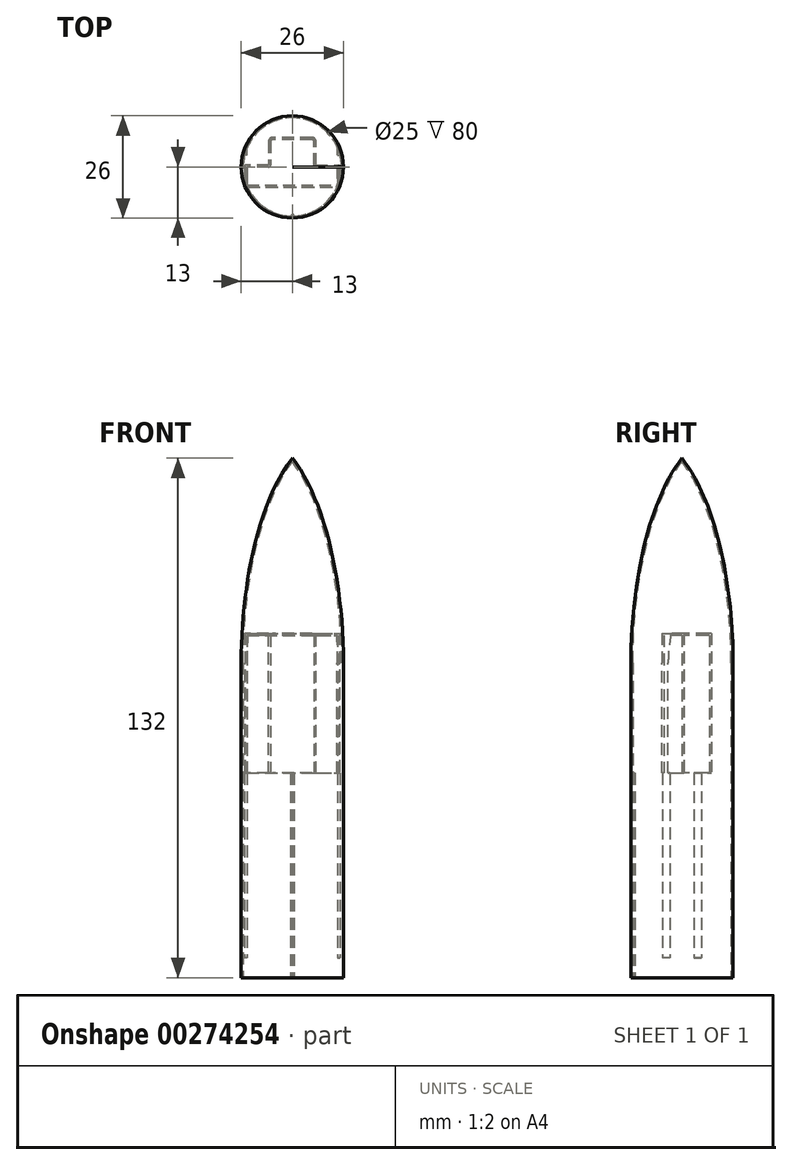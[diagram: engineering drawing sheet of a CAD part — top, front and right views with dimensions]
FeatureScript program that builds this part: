
annotation { "Feature Type Name" : "Feature", "Feature Type Description" : "" }
export const myFeature = defineFeature(function(context is Context, id is Id, definition is map)
    precondition{}
    {
        {
            var Q0;
            Q0=qCreatedBy(makeId("Top.planeOp"),FACE);
            var sketch = newSketch(context, id + "F0", { "sketchPlane" : qUnion([Q0])});
            skCircle(sketch, "E0", {"center": v(0, 0) * mm, "radius": 13 * mm});
            skSolve(sketch);
        }
        {
            var Q0;
            Q0=qCreatedBy(makeId("Front.planeOp"),FACE);
            var sketch = newSketch(context, id + "F1", { "sketchPlane" : qUnion([Q0])});
            skLineSegment(sketch, "E1", {"start": v(13, -80) * mm, "end": v(13, 0) * mm});
            skFitSpline(sketch, "E2", {"points": [v(13, 0) * mm, v(0, 52) * mm], "startDerivative": vector(0, 61.89) * mm, "endDerivative": vector(-24.62, 30.86) * mm});
            skLineSegment(sketch, "E3", {"start": v(0, 52) * mm, "end": v(0, 0) * mm});
            skLineSegment(sketch, "E4", {"start": v(13, -80) * mm, "end": v(0, -80) * mm});
            skLineSegment(sketch, "E5", {"start": v(0, 0) * mm, "end": v(0, -80) * mm});
            skSolve(sketch);
        }
        {
            var Q0;
            Q0 = qSketchRegion(id + "F1", true);
            var Q1;
            Q1=sQuery(id+"F1.wireOp",EDGE,"E3");
            revolve(context, id + "F2", {"entities" : qUnion([Q0]), "axis" : qUnion([Q1]), "revolveType" : RevolveType.FULL});
        }
        {
            var Q0;
            Q0=makeQuery(id+"F2.opRevolve","SWEPT_FACE",FACE,{"disambiguationData":[OSD([sQuery(id+"F1.wireOp",EDGE,"E4")])]});
            var sketch = newSketch(context, id + "F3", { "sketchPlane" : qUnion([Q0])});
            skCircle(sketch, "E6", {"center": v(0, 0) * mm, "radius": 4.6 * mm, "construction": true});
            skLineSegment(sketch, "E7", {"start": v(11.62, -4.6) * mm, "end": v(11.5, -4.6) * mm});
            skLineSegment(sketch, "E8", {"start": v(-11.62, 4.6) * mm, "end": v(-11.5, 4.6) * mm});
            skCircle(sketch, "E9", {"center": v(0, 0) * mm, "radius": 12.5 * mm});
            skLineSegment(sketch, "E10", {"start": v(0, 0) * mm, "end": v(11.5, 0) * mm});
            skLineSegment(sketch, "E11", {"start": v(0, 0) * mm, "end": v(-11.5, 0) * mm});
            skLineSegment(sketch, "E12", {"start": v(11.5, 3) * mm, "end": v(5.5, 3) * mm});
            skLineSegment(sketch, "E13", {"start": v(-11.5, 3) * mm, "end": v(-11.5, 0) * mm});
            skLineSegment(sketch, "E14", {"start": v(-11.5, 3) * mm, "end": v(-11.5, 4.6) * mm});
            skLineSegment(sketch, "E15", {"start": v(11.5, 3) * mm, "end": v(11.5, 0) * mm});
            skLineSegment(sketch, "E16", {"start": v(11.5, 3) * mm, "end": v(11.5, 4.6) * mm});
            skLineSegment(sketch, "E17", {"start": v(11.5, 0) * mm, "end": v(11.5, -3) * mm});
            skLineSegment(sketch, "E18", {"start": v(11.5, -3) * mm, "end": v(11.5, -4.6) * mm});
            skLineSegment(sketch, "E19", {"start": v(11.5, -3) * mm, "end": v(-11.5, -3) * mm, "construction": true});
            skLineSegment(sketch, "E20", {"start": v(-11.5, -3) * mm, "end": v(-11.5, 0) * mm});
            skLineSegment(sketch, "E21", {"start": v(-11.5, -3) * mm, "end": v(-11.5, -4.6) * mm});
            skCircle(sketch, "E22", {"center": v(0, 0) * mm, "radius": 13 * mm});
            skLineSegment(sketch, "E23", {"start": v(5.5, 3) * mm, "end": v(5.5, -7) * mm});
            skLineSegment(sketch, "E24", {"start": v(5.5, -7) * mm, "end": v(-5.5, -7) * mm});
            skLineSegment(sketch, "E25", {"start": v(-5.5, -7) * mm, "end": v(-5.5, 3) * mm});
            skLineSegment(sketch, "E26", {"start": v(0, 3) * mm, "end": v(-5.5, 3) * mm});
            skLineSegment(sketch, "E27", {"start": v(5.5, 3) * mm, "end": v(0, 3) * mm});
            skLineSegment(sketch, "E28", {"start": v(-5.5, 3) * mm, "end": v(-11.5, 3) * mm});
            skLineSegment(sketch, "E29", {"start": v(-11.5, 4.6) * mm, "end": v(-8.96, 4.6) * mm});
            skLineSegment(sketch, "E30", {"start": v(-11.5, -4.6) * mm, "end": v(-11.62, -4.6) * mm});
            skLineSegment(sketch, "E31", {"start": v(11.5, 4.6) * mm, "end": v(11.62, 4.6) * mm});
            skLineSegment(sketch, "E32", {"start": v(11.5, -4.6) * mm, "end": v(-11.5, -4.6) * mm});
            skLineSegment(sketch, "E33", {"start": v(8.96, 4.6) * mm, "end": v(11.5, 4.6) * mm});
            skLineSegment(sketch, "E34", {"start": v(-8.96, 4.6) * mm, "end": v(8.96, 4.6) * mm});
            skLineSegment(sketch, "E35", {"start": v(11.5, 0) * mm, "end": v(12.5, 0) * mm});
            skLineSegment(sketch, "E36", {"start": v(-11.5, 0) * mm, "end": v(-12.5, 0) * mm});
            skLineSegment(sketch, "E37", {"start": v(8.96, 4.6) * mm, "end": v(8.96, 5.6) * mm});
            skLineSegment(sketch, "E38", {"start": v(8.96, 5.6) * mm, "end": v(11.18, 5.6) * mm});
            skLineSegment(sketch, "E39", {"start": v(-8.96, 4.6) * mm, "end": v(-8.96, 5.6) * mm});
            skLineSegment(sketch, "E40", {"start": v(-8.96, 5.6) * mm, "end": v(-11.18, 5.6) * mm});
            skLineSegment(sketch, "E41", {"start": v(-11.5, -4.6) * mm, "end": v(-11.5, -4.9) * mm});
            skLineSegment(sketch, "E42", {"start": v(11.5, -4.6) * mm, "end": v(11.5, -4.9) * mm});
            skLineSegment(sketch, "E43", {"start": v(0, 12) * mm, "end": v(0.5, 12.5) * mm});
            skLineSegment(sketch, "E44", {"start": v(0.5, 12.5) * mm, "end": v(-0.5, 12.5) * mm});
            skLineSegment(sketch, "E45", {"start": v(-0.5, 12.5) * mm, "end": v(0, 12) * mm});
            skLineSegment(sketch, "E46", {"start": v(0, 0) * mm, "end": v(0, 12.5) * mm, "construction": true});
            skLineSegment(sketch, "E47", {"start": v(-11.5, 4.6) * mm, "end": v(-11.5, 4.9) * mm});
            skLineSegment(sketch, "E48", {"start": v(11.5, 4.6) * mm, "end": v(11.5, 4.9) * mm});
            skLineSegment(sketch, "E49", {"start": v(11.5, -3) * mm, "end": v(12.13, -3) * mm});
            skLineSegment(sketch, "E50", {"start": v(11.5, 3) * mm, "end": v(12.13, 3) * mm});
            skLineSegment(sketch, "E51", {"start": v(-11.5, -3) * mm, "end": v(-12.13, -3) * mm});
            skLineSegment(sketch, "E52", {"start": v(-11.5, 3) * mm, "end": v(-12.13, 3) * mm});
            skSolve(sketch);
        }
        {
            var Q0;
            Q0=makeQuery(id+"F3.imprint","IMPRINT",FACE,{"disambiguationData":[TD([[makeQuery(id+"F3.imprint","IMPRINT",EDGE,{"derivedFrom":sQuery(id+"F3.wireOp",EDGE,"E12")}),-1.0]])]});
            var Q1;
            {var subQ0=sQuery(id+"F3.wireOp",EDGE,"E13");Q1=makeQuery(id+"F3.imprint","IMPRINT",FACE,{"disambiguationData":[TD([[makeQuery(id+"F3.imprint","IMPRINT",EDGE,{"derivedFrom":subQ0}),1.0]])]});}
            var Q2;
            {var subQ4=sQuery(id+"F3.wireOp",EDGE,"E12");Q2=makeQuery(id+"F3.imprint","IMPRINT",FACE,{"disambiguationData":[TD([[makeQuery(id+"F3.imprint","IMPRINT",EDGE,{"derivedFrom":subQ4}),1.0]])]});}
            var Q3;
            {var subQ0=sQuery(id+"F3.wireOp",EDGE,"E26");Q3=makeQuery(id+"F3.imprint","IMPRINT",FACE,{"disambiguationData":[TD([[makeQuery(id+"F3.imprint","IMPRINT",EDGE,{"derivedFrom":subQ0}),1.0]])]});}
            var Q4;
            {var subQ1=sQuery(id+"F3.wireOp",EDGE,"E10");var subQ7=sQuery(id+"F3.wireOp",EDGE,"E11");var subQ8=makeQuery(id+"F3.imprint","INTERSECT",VERTEX,{"derivedFrom":[subQ1,subQ7]});Q4=makeQuery(id+"F3.imprint","IMPRINT",FACE,{"disambiguationData":[TD([[makeQuery(id+"F3.imprint","IMPRINT",EDGE,{"disambiguationData":[TD([[subQ8,-1.0]])],"derivedFrom":subQ1}),-1.0]])]});}
            var Q5;
            {var subQ0=sQuery(id+"F3.wireOp",EDGE,"E23");var subQ1=sQuery(id+"F3.wireOp",EDGE,"E19");var subQ2=makeQuery(id+"F3.imprint","INTERSECT",VERTEX,{"derivedFrom":[subQ1,subQ0]});Q5=makeQuery(id+"F3.imprint","IMPRINT",FACE,{"disambiguationData":[TD([[makeQuery(id+"F3.imprint","IMPRINT",EDGE,{"disambiguationData":[TD([[subQ2,-1.0]])],"derivedFrom":subQ1}),1.0]])]});}
            var Q6;
            {var subQ0=sQuery(id+"F3.wireOp",EDGE,"E24");Q6=makeQuery(id+"F3.imprint","IMPRINT",FACE,{"disambiguationData":[TD([[makeQuery(id+"F3.imprint","IMPRINT",EDGE,{"derivedFrom":subQ0}),-1.0]])]});}
            var Q7;
            {var subQ0=sQuery(id+"F3.wireOp",EDGE,"qLuiB2uP-4wZ7-qQD2-egaY-P2IEysGGcevB");Q7=makeQuery(id+"F3.imprint","IMPRINT",FACE,{"disambiguationData":[TD([[makeQuery(id+"F3.imprint","IMPRINT",EDGE,{"derivedFrom":subQ0}),-1.0]])]});}
            extrude(context, id + "F4", {"entities" : qUnion([Q0, Q1, Q2, Q3, Q4, Q5, Q6, Q7]), "operationType" : NewBodyOperationType.REMOVE, "oppositeDirection" : true, "depth" : 87 * mm});
        }
        {
            var Q0;
            {var subQ0=sQuery(id+"F3.wireOp",EDGE,"E17");Q0=makeQuery(id+"F3.imprint","IMPRINT",FACE,{"disambiguationData":[TD([[makeQuery(id+"F3.imprint","IMPRINT",EDGE,{"derivedFrom":subQ0}),-1.0]])]});}
            var Q1;
            {var subQ0=sQuery(id+"F3.wireOp",EDGE,"E18");Q1=makeQuery(id+"F3.imprint","IMPRINT",FACE,{"disambiguationData":[TD([[makeQuery(id+"F3.imprint","IMPRINT",EDGE,{"derivedFrom":subQ0}),-1.0]])]});}
            var Q2;
            {var subQ0=sQuery(id+"F3.wireOp",EDGE,"E20");Q2=makeQuery(id+"F3.imprint","IMPRINT",FACE,{"disambiguationData":[TD([[makeQuery(id+"F3.imprint","IMPRINT",EDGE,{"derivedFrom":subQ0}),-1.0]])]});}
            var Q3;
            {var subQ0=sQuery(id+"F3.wireOp",EDGE,"E21");Q3=makeQuery(id+"F3.imprint","IMPRINT",FACE,{"disambiguationData":[TD([[makeQuery(id+"F3.imprint","IMPRINT",EDGE,{"derivedFrom":subQ0}),1.0]])]});}
            var Q4;
            {var subQ1=sQuery(id+"F3.wireOp",EDGE,"E24");Q4=makeQuery(id+"F3.imprint","IMPRINT",FACE,{"disambiguationData":[TD([[makeQuery(id+"F3.imprint","IMPRINT",EDGE,{"derivedFrom":subQ1}),1.0]])]});}
            var Q5;
            Q5=makeQuery(id+"F3.imprint","IMPRINT",FACE,{"disambiguationData":[TD([[makeQuery(id+"F3.imprint","IMPRINT",EDGE,{"derivedFrom":sQuery(id+"F3.wireOp",EDGE,"E33")}),1.0]])]});
            var Q6;
            Q6=makeQuery(id+"F3.imprint","IMPRINT",FACE,{"disambiguationData":[TD([[makeQuery(id+"F3.imprint","IMPRINT",EDGE,{"derivedFrom":sQuery(id+"F3.wireOp",EDGE,"E29")}),1.0]])]});
            var Q7;
            Q7=makeQuery(id+"F3.imprint","IMPRINT",FACE,{"disambiguationData":[TD([[makeQuery(id+"F3.imprint","IMPRINT",EDGE,{"derivedFrom":sQuery(id+"F3.wireOp",EDGE,"E34")}),1.0]])]});
            var Q8;
            Q8=makeQuery(id+"F3.imprint","IMPRINT",FACE,{"disambiguationData":[TD([[makeQuery(id+"F3.imprint","IMPRINT",EDGE,{"derivedFrom":sQuery(id+"F3.wireOp",EDGE,"E15")}),1.0]])]});
            var Q9;
            Q9=makeQuery(id+"F3.imprint","IMPRINT",FACE,{"disambiguationData":[TD([[makeQuery(id+"F3.imprint","IMPRINT",EDGE,{"derivedFrom":sQuery(id+"F3.wireOp",EDGE,"E20")}),1.0]])]});
            var Q10;
            Q10=makeQuery(id+"F3.imprint","IMPRINT",FACE,{"disambiguationData":[TD([[makeQuery(id+"F3.imprint","IMPRINT",EDGE,{"derivedFrom":sQuery(id+"F3.wireOp",EDGE,"E17")}),1.0]])]});
            var Q11;
            Q11=makeQuery(id+"F3.imprint","IMPRINT",FACE,{"disambiguationData":[TD([[makeQuery(id+"F3.imprint","IMPRINT",EDGE,{"derivedFrom":sQuery(id+"F3.wireOp",EDGE,"E13")}),-1.0]])]});
            extrude(context, id + "F5", {"entities" : qUnion([Q0, Q1, Q2, Q3, Q4, Q5, Q6, Q7, Q8, Q9, Q10, Q11]), "operationType" : NewBodyOperationType.REMOVE, "oppositeDirection" : true, "depth" : 52 * mm});
        }
        {
            var Q0;
            {var subQ2=sQuery(id+"F3.wireOp",EDGE,"E7");Q0=makeQuery(id+"F3.imprint","IMPRINT",FACE,{"disambiguationData":[TD([[makeQuery(id+"F3.imprint","IMPRINT",EDGE,{"derivedFrom":subQ2}),1.0]])]});}
            var Q1;
            {var subQ1=sQuery(id+"F3.wireOp",EDGE,"E8");Q1=makeQuery(id+"F3.imprint","IMPRINT",FACE,{"disambiguationData":[TD([[makeQuery(id+"F3.imprint","IMPRINT",EDGE,{"derivedFrom":subQ1}),-1.0]])]});}
            var Q2;
            {var subQ1=sQuery(id+"F3.wireOp",EDGE,"E7");Q2=makeQuery(id+"F3.imprint","IMPRINT",FACE,{"disambiguationData":[TD([[makeQuery(id+"F3.imprint","IMPRINT",EDGE,{"derivedFrom":subQ1}),-1.0]])]});}
            var Q3;
            {var subQ0=sQuery(id+"F3.wireOp",EDGE,"E30");Q3=makeQuery(id+"F3.imprint","IMPRINT",FACE,{"disambiguationData":[TD([[makeQuery(id+"F3.imprint","IMPRINT",EDGE,{"derivedFrom":subQ0}),1.0]])]});}
            var Q4;
            {var subQ0=sQuery(id+"F3.wireOp",EDGE,"E31");Q4=makeQuery(id+"F3.imprint","IMPRINT",FACE,{"disambiguationData":[TD([[makeQuery(id+"F3.imprint","IMPRINT",EDGE,{"derivedFrom":subQ0}),1.0]])]});}
            var Q5;
            {var subQ0=sQuery(id+"F3.wireOp",EDGE,"E8");Q5=makeQuery(id+"F3.imprint","IMPRINT",FACE,{"disambiguationData":[TD([[makeQuery(id+"F3.imprint","IMPRINT",EDGE,{"derivedFrom":subQ0}),1.0]])]});}
            var Q6;
            Q6=makeQuery(id+"F3.imprint","IMPRINT",FACE,{"disambiguationData":[TD([[makeQuery(id+"F3.imprint","IMPRINT",EDGE,{"derivedFrom":sQuery(id+"F3.wireOp",EDGE,"E16")}),-1.0]])]});
            var Q7;
            Q7=makeQuery(id+"F3.imprint","IMPRINT",FACE,{"disambiguationData":[TD([[makeQuery(id+"F3.imprint","IMPRINT",EDGE,{"derivedFrom":sQuery(id+"F3.wireOp",EDGE,"E21")}),-1.0]])]});
            extrude(context, id + "F6", {"entities" : qUnion([Q0, Q1, Q2, Q3, Q4, Q5, Q6, Q7]), "operationType" : NewBodyOperationType.REMOVE, "oppositeDirection" : true, "depth" : 5.08 * mm});
        }
        {
            var Q0;
            Q0=makeQuery(id+"F5.boolean.opBoolean","COPY",EDGE,{"derivedFrom":makeQuery(id+"F5.opExtrude","CAP_EDGE",EDGE,{"disambiguationData":[OSD([sQuery(id+"F3.wireOp",EDGE,"E25")])],"isStart":false})});
            var Q1;
            Q1=makeQuery(id+"F5.boolean.opBoolean","COPY",EDGE,{"derivedFrom":makeQuery(id+"F5.opExtrude","CAP_EDGE",EDGE,{"disambiguationData":[OSD([sQuery(id+"F3.wireOp",EDGE,"E24")])],"isStart":false})});
            var Q2;
            Q2=makeQuery(id+"F5.boolean.opBoolean","COPY",EDGE,{"derivedFrom":makeQuery(id+"F5.opExtrude","CAP_EDGE",EDGE,{"disambiguationData":[OSD([sQuery(id+"F3.wireOp",EDGE,"E23")])],"isStart":false})});
            var Q3;
            Q3=makeQuery(id+"F5.boolean.opBoolean","COPY",EDGE,{"derivedFrom":makeQuery(id+"F5.opExtrude","CAP_EDGE",EDGE,{"disambiguationData":[OSD([sQuery(id+"F3.wireOp",EDGE,"E11")])],"isStart":false})});
            var Q4;
            Q4=makeQuery(id+"F5.boolean.opBoolean","COPY",EDGE,{"derivedFrom":makeQuery(id+"F5.opExtrude","CAP_EDGE",EDGE,{"disambiguationData":[OSD([sQuery(id+"F3.wireOp",EDGE,"E10")])],"isStart":false})});
            var Q5;
            Q5=makeQuery(id+"F5.boolean.opBoolean","COPY",EDGE,{"derivedFrom":makeQuery(id+"F5.opExtrude","CAP_EDGE",EDGE,{"disambiguationData":[OSD([sQuery(id+"F3.wireOp",EDGE,"E29"),sQuery(id+"F3.wireOp",EDGE,"E33"),sQuery(id+"F3.wireOp",EDGE,"E34")])],"isStart":false})});
            var Q6;
            Q6=makeQuery(id+"F4.boolean.opBoolean","COPY",EDGE,{"derivedFrom":makeQuery(id+"F4.opExtrude","SWEPT_EDGE",EDGE,{"disambiguationData":[OSD([sQuery(id+"F3.wireOp",EDGE,"E10"),sQuery(id+"F3.wireOp",EDGE,"E23")])]})});
            var Q7;
            Q7=makeQuery(id+"F4.boolean.opBoolean","COPY",EDGE,{"derivedFrom":makeQuery(id+"F4.opExtrude","SWEPT_EDGE",EDGE,{"disambiguationData":[OSD([sQuery(id+"F3.wireOp",EDGE,"E11"),sQuery(id+"F3.wireOp",EDGE,"E25")])]})});
            var Q8;
            Q8=makeQuery(id+"F4.boolean.opBoolean","COPY",EDGE,{"derivedFrom":makeQuery(id+"F4.opExtrude","SWEPT_EDGE",EDGE,{"disambiguationData":[OSD([sQuery(id+"F3.wireOp",EDGE,"E24"),sQuery(id+"F3.wireOp",EDGE,"E25")])]})});
            var Q9;
            Q9=makeQuery(id+"F4.boolean.opBoolean","COPY",EDGE,{"derivedFrom":makeQuery(id+"F4.opExtrude","SWEPT_EDGE",EDGE,{"disambiguationData":[OSD([sQuery(id+"F3.wireOp",EDGE,"E23"),sQuery(id+"F3.wireOp",EDGE,"E24")])]})});
            var Q10;
            Q10=makeQuery(id+"F5.boolean.opBoolean","COPY",EDGE,{"derivedFrom":makeQuery(id+"F5.opExtrude","CAP_EDGE",EDGE,{"disambiguationData":[OSD([sQuery(id+"F3.wireOp",EDGE,"E15")])],"isStart":false})});
            var Q11;
            Q11=makeQuery(id+"F5.boolean.opBoolean","COPY",EDGE,{"derivedFrom":makeQuery(id+"F5.opExtrude","CAP_EDGE",EDGE,{"disambiguationData":[OSD([sQuery(id+"F3.wireOp",EDGE,"E13")])],"isStart":false})});
            fillet(context, id + "F7", {"entities" : qUnion([Q0, Q1, Q2, Q3, Q4, Q5, Q6, Q7, Q8, Q9, Q10, Q11]), "radius" : 0.5 * mm, "tangentPropagation" : true, "allowEdgeOverflow" : false});
        }
        {
            var Q0;
            Q0=makeQuery(id+"F5.boolean.opBoolean","COPY",FACE,{"derivedFrom":makeQuery(id+"F5.opExtrude","CAP_FACE",FACE,{"disambiguationData":[OSD([sQuery(id+"F3.wireOp",EDGE,"E9"),sQuery(id+"F3.wireOp",EDGE,"E29"),sQuery(id+"F3.wireOp",EDGE,"E33"),sQuery(id+"F3.wireOp",EDGE,"E34"),sQuery(id+"F3.wireOp",EDGE,"E43"),sQuery(id+"F3.wireOp",EDGE,"E45"),sQuery(id+"F3.wireOp",EDGE,"E47"),sQuery(id+"F3.wireOp",EDGE,"E48")])],"isStart":false})});
            var Q1;
            Q1=makeQuery(id+"F5.boolean.opBoolean","COPY",FACE,{"derivedFrom":makeQuery(id+"F5.opExtrude","CAP_FACE",FACE,{"disambiguationData":[OSD([sQuery(id+"F3.wireOp",EDGE,"E7"),sQuery(id+"F3.wireOp",EDGE,"E8"),sQuery(id+"F3.wireOp",EDGE,"E9"),sQuery(id+"F3.wireOp",EDGE,"E10"),sQuery(id+"F3.wireOp",EDGE,"E11"),sQuery(id+"F3.wireOp",EDGE,"E13"),sQuery(id+"F3.wireOp",EDGE,"E14"),sQuery(id+"F3.wireOp",EDGE,"E15"),sQuery(id+"F3.wireOp",EDGE,"E16"),sQuery(id+"F3.wireOp",EDGE,"E23"),sQuery(id+"F3.wireOp",EDGE,"E24"),sQuery(id+"F3.wireOp",EDGE,"E25"),sQuery(id+"F3.wireOp",EDGE,"E30"),sQuery(id+"F3.wireOp",EDGE,"E31"),sQuery(id+"F3.wireOp",EDGE,"E41"),sQuery(id+"F3.wireOp",EDGE,"E42")])],"isStart":false})});
            shell(context, id + "F8", {"entities" : qUnion([Q0, Q1]), "thickness" : 0.5 * mm});
        }
    });
